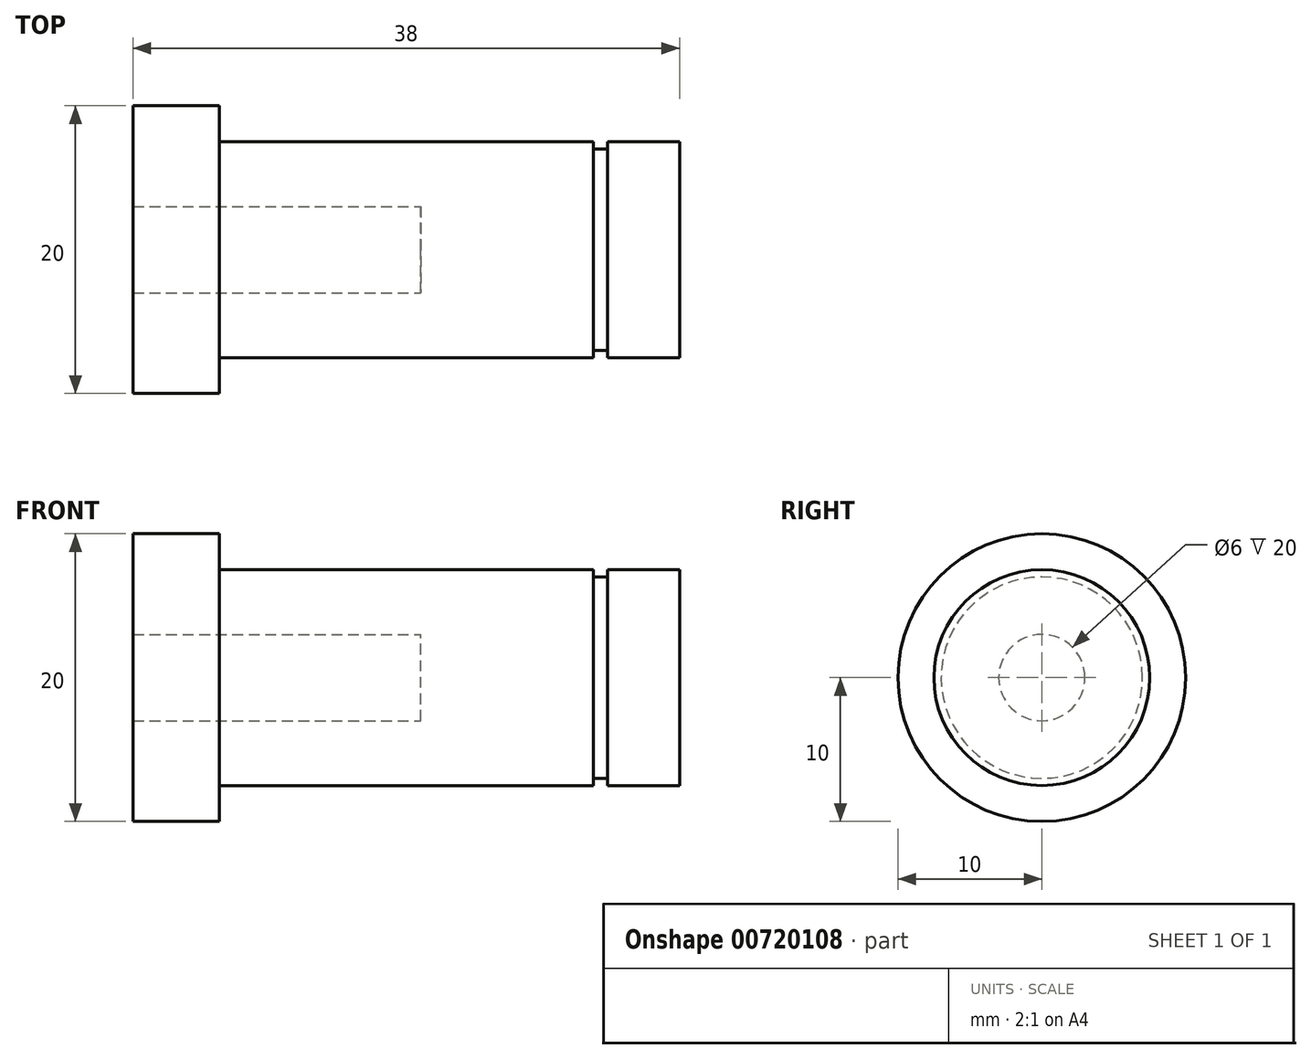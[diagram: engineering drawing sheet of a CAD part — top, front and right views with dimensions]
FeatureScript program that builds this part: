
annotation { "Feature Type Name" : "Feature", "Feature Type Description" : "" }
export const myFeature = defineFeature(function(context is Context, id is Id, definition is map)
    precondition{}
    {
        {
            var Q0;
            Q0=qCreatedBy(makeId("Front.planeOp"),FACE);
            var sketch = newSketch(context, id + "F0", { "sketchPlane" : qUnion([Q0])});
            skLineSegment(sketch, "E0", {"start": v(0, 3) * mm, "end": v(0, 10) * mm});
            skLineSegment(sketch, "E1", {"start": v(0, 10) * mm, "end": v(6, 10) * mm});
            skLineSegment(sketch, "E2", {"start": v(6, 10) * mm, "end": v(6, 7.5) * mm});
            skLineSegment(sketch, "E3", {"start": v(6, 7.5) * mm, "end": v(32, 7.5) * mm});
            skLineSegment(sketch, "E4", {"start": v(32, 7.5) * mm, "end": v(32, 7) * mm});
            skLineSegment(sketch, "E5", {"start": v(32, 7) * mm, "end": v(33, 7) * mm});
            skLineSegment(sketch, "E6", {"start": v(33, 7) * mm, "end": v(33, 7.5) * mm});
            skLineSegment(sketch, "E7", {"start": v(33, 7.5) * mm, "end": v(38, 7.5) * mm});
            skLineSegment(sketch, "E8", {"start": v(38, 7.5) * mm, "end": v(38, 0) * mm});
            skLineSegment(sketch, "E9", {"start": v(38, 0) * mm, "end": v(20, 0) * mm});
            skLineSegment(sketch, "E10.0", {"start": v(20, 3) * mm, "end": v(0, 3) * mm});
            skLineSegment(sketch, "E11.0", {"start": v(20, 0) * mm, "end": v(20, 3) * mm});
            skPoint(sketch, "E12.orphan", {"position": v(0, 0) * mm});
            skSolve(sketch);
        }
        {
            var Q0;
            Q0=makeQuery(id+"F0.imprint","IMPRINT",FACE,{"disambiguationData":[TD([[makeQuery(id+"F0.imprint","IMPRINT",EDGE,{"derivedFrom":sQuery(id+"F0.wireOp",EDGE,"E0")}),-1.0]])]});
            var Q1;
            Q1=sQuery(id+"F0.wireOp",EDGE,"E9");
            revolve(context, id + "F1", {"surfaceOperationType" : NewSurfaceOperationType.NEW, "entities" : qUnion([Q0]), "axis" : qUnion([Q1]), "revolveType" : RevolveType.FULL});
        }
    });
